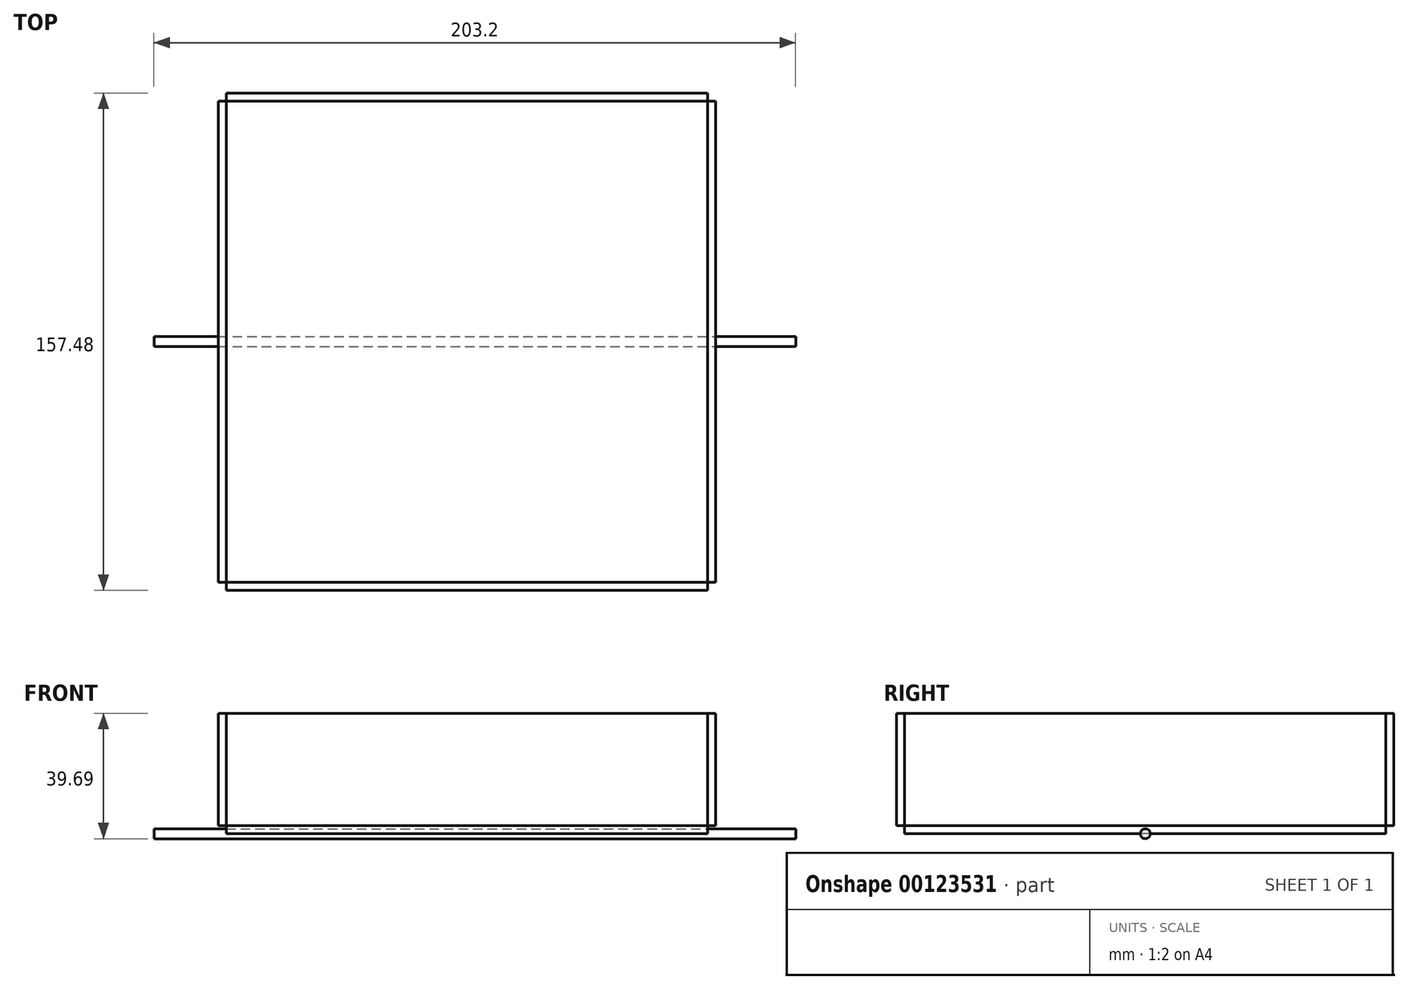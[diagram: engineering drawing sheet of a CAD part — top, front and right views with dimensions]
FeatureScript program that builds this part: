
annotation { "Feature Type Name" : "Feature", "Feature Type Description" : "" }
export const myFeature = defineFeature(function(context is Context, id is Id, definition is map)
    precondition{}
    {
        {
            var Q0;
            Q0=qCreatedBy(makeId("Top.planeOp"),FACE);
            var sketch = newSketch(context, id + "F0", { "sketchPlane" : qUnion([Q0])});
            skLineSegment(sketch, "E0.bottom", {"start": v(-105.43, 77.1) * mm, "end": v(46.97, 77.1) * mm});
            skLineSegment(sketch, "E0.top", {"start": v(-105.43, -75.3) * mm, "end": v(46.97, -75.3) * mm});
            skLineSegment(sketch, "E0.left", {"start": v(-105.43, 77.1) * mm, "end": v(-105.43, -75.3) * mm});
            skLineSegment(sketch, "E0.right", {"start": v(46.97, 77.1) * mm, "end": v(46.97, -75.3) * mm});
            skSolve(sketch);
        }
        {
            var Q0;
            Q0=makeQuery(id+"F0.imprint","IMPRINT",FACE,{"disambiguationData":[TD([[makeQuery(id+"F0.imprint","IMPRINT",EDGE,{"derivedFrom":sQuery(id+"F0.wireOp",EDGE,"E0.bottom")}),-1.0]])]});
            extrude(context, id + "F1", {"entities" : qUnion([Q0]), "depth" : 2.54 * mm});
        }
        {
            var Q0;
            Q0=makeQuery(id+"F1.opExtrude","SWEPT_FACE",FACE,{"disambiguationData":[OSD([sQuery(id+"F0.wireOp",EDGE,"E0.top")])]});
            var sketch = newSketch(context, id + "F2", { "sketchPlane" : qUnion([Q0])});
            skLineSegment(sketch, "E1.bottom", {"start": v(-105.43, 0) * mm, "end": v(46.97, 0) * mm});
            skLineSegment(sketch, "E1.top", {"start": v(-105.43, 38.1) * mm, "end": v(46.97, 38.1) * mm});
            skLineSegment(sketch, "E1.left", {"start": v(-105.43, 0) * mm, "end": v(-105.43, 38.1) * mm});
            skLineSegment(sketch, "E1.right", {"start": v(46.97, 0) * mm, "end": v(46.97, 38.1) * mm});
            skSolve(sketch);
        }
        {
            var Q0;
            {var subQ0=sQuery(id+"F2.wireOp",EDGE,"E1.top");Q0=makeQuery(id+"F2.imprint","IMPRINT",FACE,{"disambiguationData":[TD([[makeQuery(id+"F2.imprint","IMPRINT",EDGE,{"derivedFrom":subQ0}),-1.0]])]});}
            extrude(context, id + "F3", {"entities" : qUnion([Q0]), "depth" : 2.54 * mm});
        }
        {
            var Q0;
            Q0=makeQuery(id+"F3.opExtrude","SWEPT_FACE",FACE,{"disambiguationData":[OSD([sQuery(id+"F2.wireOp",EDGE,"E1.right")])]});
            var sketch = newSketch(context, id + "F4", { "sketchPlane" : qUnion([Q0])});
            skLineSegment(sketch, "E2.bottom", {"start": v(-75.3, 2.54) * mm, "end": v(77.1, 2.54) * mm});
            skLineSegment(sketch, "E2.top", {"start": v(-75.3, 38.1) * mm, "end": v(77.1, 38.1) * mm});
            skLineSegment(sketch, "E2.left", {"start": v(-75.3, 2.54) * mm, "end": v(-75.3, 38.1) * mm});
            skLineSegment(sketch, "E2.right", {"start": v(77.1, 2.54) * mm, "end": v(77.1, 38.1) * mm});
            skSolve(sketch);
        }
        {
            var Q0;
            Q0=makeQuery(id+"F4.imprint","IMPRINT",FACE,{"disambiguationData":[TD([[makeQuery(id+"F4.imprint","IMPRINT",EDGE,{"derivedFrom":sQuery(id+"F4.wireOp",EDGE,"E2.bottom")}),1.0]])]});
            extrude(context, id + "F5", {"entities" : qUnion([Q0]), "depth" : 2.54 * mm});
        }
        {
            var Q0;
            Q0=makeQuery(id+"F5.opExtrude","SWEPT_FACE",FACE,{"disambiguationData":[OSD([sQuery(id+"F4.wireOp",EDGE,"E2.right")])]});
            var sketch = newSketch(context, id + "F6", { "sketchPlane" : qUnion([Q0])});
            skLineSegment(sketch, "E3.bottom", {"start": v(-46.97, 2.54) * mm, "end": v(105.43, 2.54) * mm});
            skLineSegment(sketch, "E3.top", {"start": v(-46.97, 38.1) * mm, "end": v(105.43, 38.1) * mm});
            skLineSegment(sketch, "E3.left", {"start": v(-46.97, 2.54) * mm, "end": v(-46.97, 38.1) * mm});
            skLineSegment(sketch, "E3.right", {"start": v(105.43, 2.54) * mm, "end": v(105.43, 38.1) * mm});
            skSolve(sketch);
        }
        {
            var Q0;
            Q0=makeQuery(id+"F6.imprint","IMPRINT",FACE,{"disambiguationData":[TD([[makeQuery(id+"F6.imprint","IMPRINT",EDGE,{"derivedFrom":sQuery(id+"F6.wireOp",EDGE,"E3.bottom")}),1.0]])]});
            extrude(context, id + "F7", {"entities" : qUnion([Q0]), "depth" : 2.54 * mm});
        }
        {
            var Q0;
            Q0=makeQuery(id+"F7.opExtrude","SWEPT_FACE",FACE,{"disambiguationData":[OSD([sQuery(id+"F6.wireOp",EDGE,"E3.right")])]});
            var sketch = newSketch(context, id + "F8", { "sketchPlane" : qUnion([Q0])});
            skLineSegment(sketch, "E4.bottom", {"start": v(-77.1, 2.54) * mm, "end": v(75.3, 2.54) * mm});
            skLineSegment(sketch, "E4.top", {"start": v(-77.1, 38.1) * mm, "end": v(75.3, 38.1) * mm});
            skLineSegment(sketch, "E4.left", {"start": v(-77.1, 2.54) * mm, "end": v(-77.1, 38.1) * mm});
            skLineSegment(sketch, "E4.right", {"start": v(75.3, 2.54) * mm, "end": v(75.3, 38.1) * mm});
            skSolve(sketch);
        }
        {
            var Q0;
            Q0=makeQuery(id+"F8.imprint","IMPRINT",FACE,{"disambiguationData":[TD([[makeQuery(id+"F8.imprint","IMPRINT",EDGE,{"derivedFrom":sQuery(id+"F8.wireOp",EDGE,"E4.bottom")}),1.0]])]});
            extrude(context, id + "F9", {"entities" : qUnion([Q0]), "depth" : 2.54 * mm});
        }
        {
            var Q0;
            Q0=makeQuery(id+"F5.opExtrude","CAP_FACE",FACE,{"disambiguationData":[OSD([sQuery(id+"F4.wireOp",EDGE,"E2.bottom"),sQuery(id+"F4.wireOp",EDGE,"E2.top"),sQuery(id+"F4.wireOp",EDGE,"E2.left"),sQuery(id+"F4.wireOp",EDGE,"E2.right")])],"isStart":false});
            var sketch = newSketch(context, id + "F10", { "sketchPlane" : qUnion([Q0])});
            skCircle(sketch, "E5", {"center": v(0.9, 0) * mm, "radius": 1.59 * mm});
            skSolve(sketch);
        }
        {
            var Q0;
            Q0=makeQuery(id+"F10.imprint","IMPRINT",FACE,{"disambiguationData":[TD([[makeQuery(id+"F10.imprint","IMPRINT",EDGE,{"derivedFrom":sQuery(id+"F10.wireOp",EDGE,"E5")}),1.0]])]});
            extrude(context, id + "F11", {"entities" : qUnion([Q0]), "oppositeDirection" : true, "depth" : 177.8 * mm, "hasSecondDirection" : true, "secondDirectionOppositeDirection" : false, "secondDirectionDepth" : 25.4 * mm});
        }
    });
